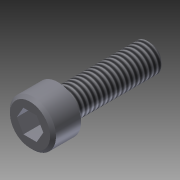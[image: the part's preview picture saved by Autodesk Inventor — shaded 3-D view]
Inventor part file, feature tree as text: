
AUTODESK INVENTOR PART (.ipt)
format: ipt  version: 2013 (Build 170138000, 138)  size: 109,568 bytes
history: native  units: in
note: dims shown in document units (in); Inventor stores cm internally (conversion verified against a paired STEP export)
features: extrude x3, sketch x3, chamfer x2, thread x1
ambient origin geometry x8: Origin, YZ Plane, XZ Plane, XY Plane, X Axis, Y Axis, Z Axis, Center Point
bodies: Solid1 (feature_tree)
feature tree (9):
  extrude  "Extrusion1"  Depth=0.19in TaperAngle=0.0deg
  extrude  "Extrusion2"  Depth=0.625in TaperAngle=0.0deg
  extrude  "Extrusion3"  Depth=0.125in TaperAngle=0.0deg
  thread  "Thread1"  [1 undecoded]
  chamfer  "Chamfer1"  Distance=0.02in Angle=45.0deg
  chamfer  "Chamfer2"  Distance=0.02in Angle=45.0deg
  sketch  "Sketch1"  dims[d0=0.312in d1=0.19in d2=0.0in]
  sketch  "Sketch2"  dims[d3=0.19in d4=0.625in d5=0.0in]
  sketch  "Sketch3"  dims[d6=0.1562in d7=0.125in d8=0.0in d9=1.0in d10=0.0in d11=0.02in d12=0.125in d13=45.0deg d14=0.02in d15=0.125in d16=45.0deg]
note: 1 required parameter value undecoded (feature->parameter linkage not recoverable at this tier; creation-order binding heuristic only, values carry confidence <= 0.55)
